# Revit family: IS_Connect_Multiproduct_BIM_DE_E5049
name_source: partatom
category: Plumbing Fixtures
revit_build: Autodesk Revit 2016 (Build: 20150220_1215(x64)
units: mm (PartAtom-declared; Revit-internal decimal feet)

## family parameters
Cut with Voids When Loaded = Yes
Host = Face
OmniClass Number = 23.45.05.14.14
OmniClass Title = Sinks/Lavatories
Part Type = Normal
Room Calculation Point = No
Round Connector Dimension = Use Diameter
Shared = Yes

## types (1)
- E504901 - CONNECT LAVABO INC.62X42 S/FOR OVALE BEU
    Accessories = www.idealstandard.de\ersatzteile
    AreaUnits = millimeters
    Assembly Code = C1030200
    AssetType = Fixed
    BIMObjectName = ISI_IdealStandard_Sinks_CONNECT_E504901
    BIMobject category = Basins
    BarCode = 5017830446934
    Brand url = http://www.idealstandard.co.uk
    CWFU = 0
    CodePerformance = DIN EN 14688 CL 15, DIN EN 31
    Color = White
    ConnectionType = Plumbing
    Cost = 0 $
    CurrencyUnit = €
    Date of publishing = 6/23/2017
    Default Elevation = 864 mm  [stored 2.83465 ft]
    DurationUnit = year
    EAN code = https://5017830446934
    Edition number = 1
    ExpectedLife = 25
    Features = CONNECT countertop washbasin 620x410mm, no taphole, with overflow
    Finish = White
    GrossWeight = 9 kg
    HWFU = 0
    IFC Classification = Sanitary Terminal
    Installation instructions = http://www.idealstandard.de
    InstallationDate = 1900-12-31T23:59:59
    InstallationInstructions = www.idealstandard.de\produkte
    LinearUnits = millimeters
    Manufacturer name = Ideal Standard
    ManufacturerURL = www.idealstandard.de
    Material = Vitreous china
    Material main = Ceramics
    Model = E504901
    ModelNumber = E504901
    ModelReference = IS Einbauwaschtisch CONNECT, oval, o.Hl., m.Ül., 620x410x175mm, Weiß
    NBS Reference Code = 35-79-18
    NBS Reference Description = Counter Top Wash Basins
    Name = ISI_IdealStandard_Sinks_CONNECT_E504901
    Nominal height = 175 mm
    Nominal width = 620 mm
    NominalDepth = 0 mm  [stored 0 ft]
    NominalLength = 410 mm
    OmniClass Code = 23-31 13 00
    OmniClass Description = Sinks
    Product Guid = 2821fba6-a6fe-4440-b94f-751cd5d5af36
    Product SKU = E5049
    Product data url = https://bimobject.com
    Product family = CONNECT
    Product group = Basin
    Product url = http://www.idealstandard.de
    ProductInformation = www.idealstandard.de
    QR code = http://bimobject.com
    Shape = Sculptured
    Size = 620 x 410 x 175 mm
    Space = Internal
    Technical description = http://www.idealstandard.de
    URL = www.idealstandard.de
    Uniclass 1.4 Code = L7212
    Uniclass 1.4 Description = Washbasins
    Uniclass 2.0 Code = PR-35-79-94
    Uniclass 2.0 Description = Wall-Hung Wash Basins
    Uniclass 2015 Code = Pr_40_20_96_96
    Uniclass 2015 Name = Wall-hung wash basins
    Uniclass2015Code = Pr_40_20_96_18
    Uniclass2015Title = Counter top wash basins
    Uniclass2015Version = Products v1.1
    Version = 1
    VolumeUnits = Litres
    WFU = 0
    WasteCover = ISI_IdealStandard_BasinMaterial_White3_Render
    Weight Net (Kg) = 7.32

note: [stored X ft] marks values corroborated as IEEE doubles in the binary element streams (Revit-internal decimal feet)

## geometry (parser evidence)
native form markers: Blend x8, Sweep x2
no freeform markers — native parametric forms only
